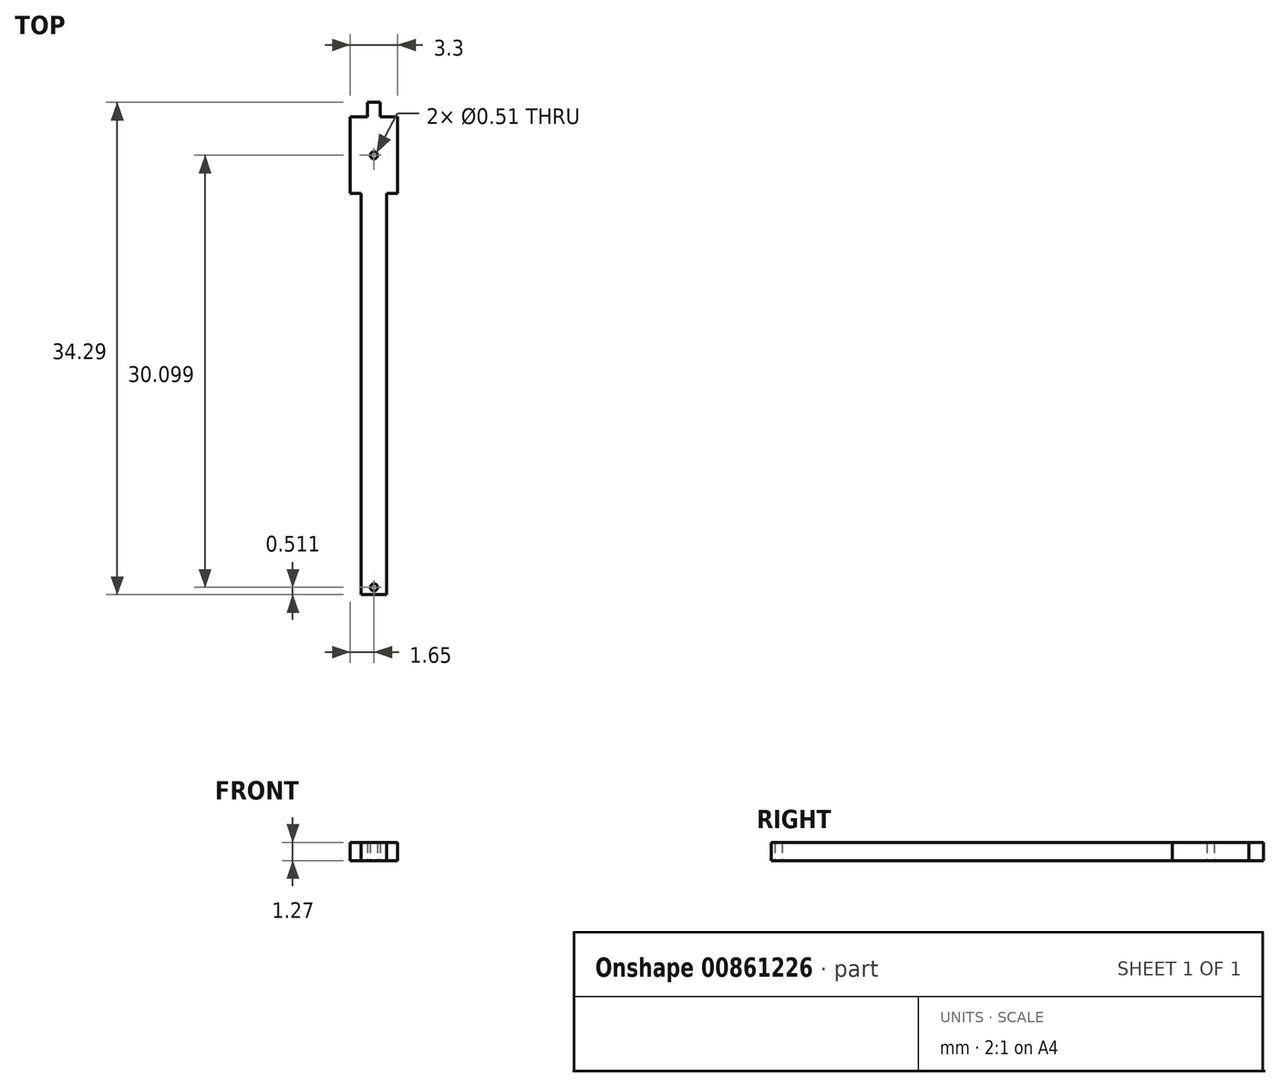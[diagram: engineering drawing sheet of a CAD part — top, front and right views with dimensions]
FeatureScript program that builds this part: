
annotation { "Feature Type Name" : "Feature", "Feature Type Description" : "" }
export const myFeature = defineFeature(function(context is Context, id is Id, definition is map)
    precondition{}
    {
        {
            var Q0;
            Q0=qCreatedBy(makeId("Top.planeOp"),FACE);
            var sketch = newSketch(context, id + "F0", { "sketchPlane" : qUnion([Q0])});
            skLineSegment(sketch, "E0.bottom", {"start": v(1.65, -2.67) * mm, "end": v(0.89, -2.67) * mm});
            skLineSegment(sketch, "E0.top", {"start": v(1.65, 2.67) * mm, "end": v(-1.65, 2.67) * mm});
            skLineSegment(sketch, "E0.left", {"start": v(1.65, -2.67) * mm, "end": v(1.65, 2.67) * mm});
            skLineSegment(sketch, "E0.right", {"start": v(-1.65, -2.67) * mm, "end": v(-1.65, 2.67) * mm});
            skPoint(sketch, "E0.middle", {"position": v(0, 0) * mm});
            skLineSegment(sketch, "E1.top", {"start": v(-0.89, -30.6) * mm, "end": v(0.89, -30.6) * mm});
            skLineSegment(sketch, "E1.left", {"start": v(-0.89, -2.67) * mm, "end": v(-0.89, -30.6) * mm});
            skLineSegment(sketch, "E1.right", {"start": v(0.89, -2.67) * mm, "end": v(0.89, -30.6) * mm});
            skCircle(sketch, "E2", {"center": v(0, -30.1) * mm, "radius": 0.25 * mm});
            skLineSegment(sketch, "E3.trimOffspring", {"start": v(-0.89, -2.67) * mm, "end": v(-1.65, -2.67) * mm});
            skCircle(sketch, "E4", {"center": v(0, 0) * mm, "radius": 0.25 * mm});
            skLineSegment(sketch, "E5.bottom", {"start": v(-0.44, 2.67) * mm, "end": v(0.44, 2.67) * mm});
            skLineSegment(sketch, "E5.top", {"start": v(-0.44, 3.68) * mm, "end": v(0.44, 3.68) * mm});
            skLineSegment(sketch, "E5.left", {"start": v(-0.44, 2.67) * mm, "end": v(-0.44, 3.68) * mm});
            skLineSegment(sketch, "E5.right", {"start": v(0.44, 2.67) * mm, "end": v(0.44, 3.68) * mm});
            skSolve(sketch);
        }
        {
            var Q0;
            {Q0=qUnion([makeQuery(id+"F0.imprint","IMPRINT",FACE,{"disambiguationData":[TD([[makeQuery(id+"F0.imprint","IMPRINT",EDGE,{"derivedFrom":sQuery(id+"F0.wireOp",EDGE,"E0.bottom")}),-1.0]])]}),makeQuery(id+"F0.imprint","IMPRINT",FACE,{"disambiguationData":[TD([[makeQuery(id+"F0.imprint","IMPRINT",EDGE,{"derivedFrom":sQuery(id+"F0.wireOp",EDGE,"E5.top")}),-1.0]])]})]);}
            extrude(context, id + "F1", {"entities" : qUnion([Q0]), "depth" : 1.27 * mm, "offsetDistance" : 25.4 * mm});
        }
    });
